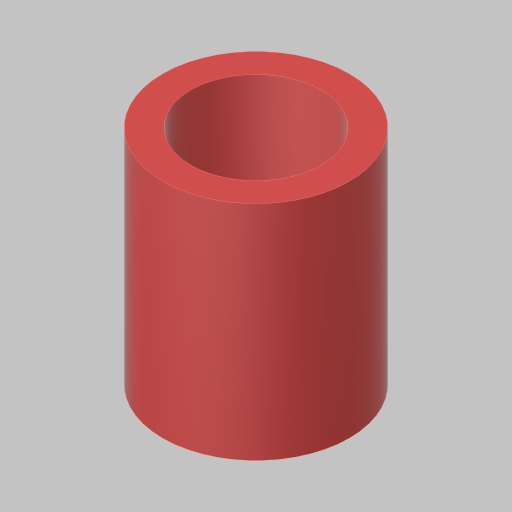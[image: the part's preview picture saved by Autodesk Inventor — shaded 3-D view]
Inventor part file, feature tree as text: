
AUTODESK INVENTOR PART (.ipt)
format: ipt  version: 2023.5 (Build 275446000, 446)  size: 102,400 bytes
history: native  units: in
note: dims shown in document units (in); Inventor stores cm internally (conversion verified against a paired STEP export)
features: extrude x1, sketch x1
ambient origin geometry x8: Origin, YZ Plane, XZ Plane, XY Plane, X Axis, Y Axis, Z Axis, Center Point
bodies: Solid1 (feature_tree)
feature tree (2):
  extrude  "Extrusion1"  Depth=0.99in
  sketch  "Sketch1"  dims[d0=0.58in d1=0.125in d2=0.99in d3=0.0in]
